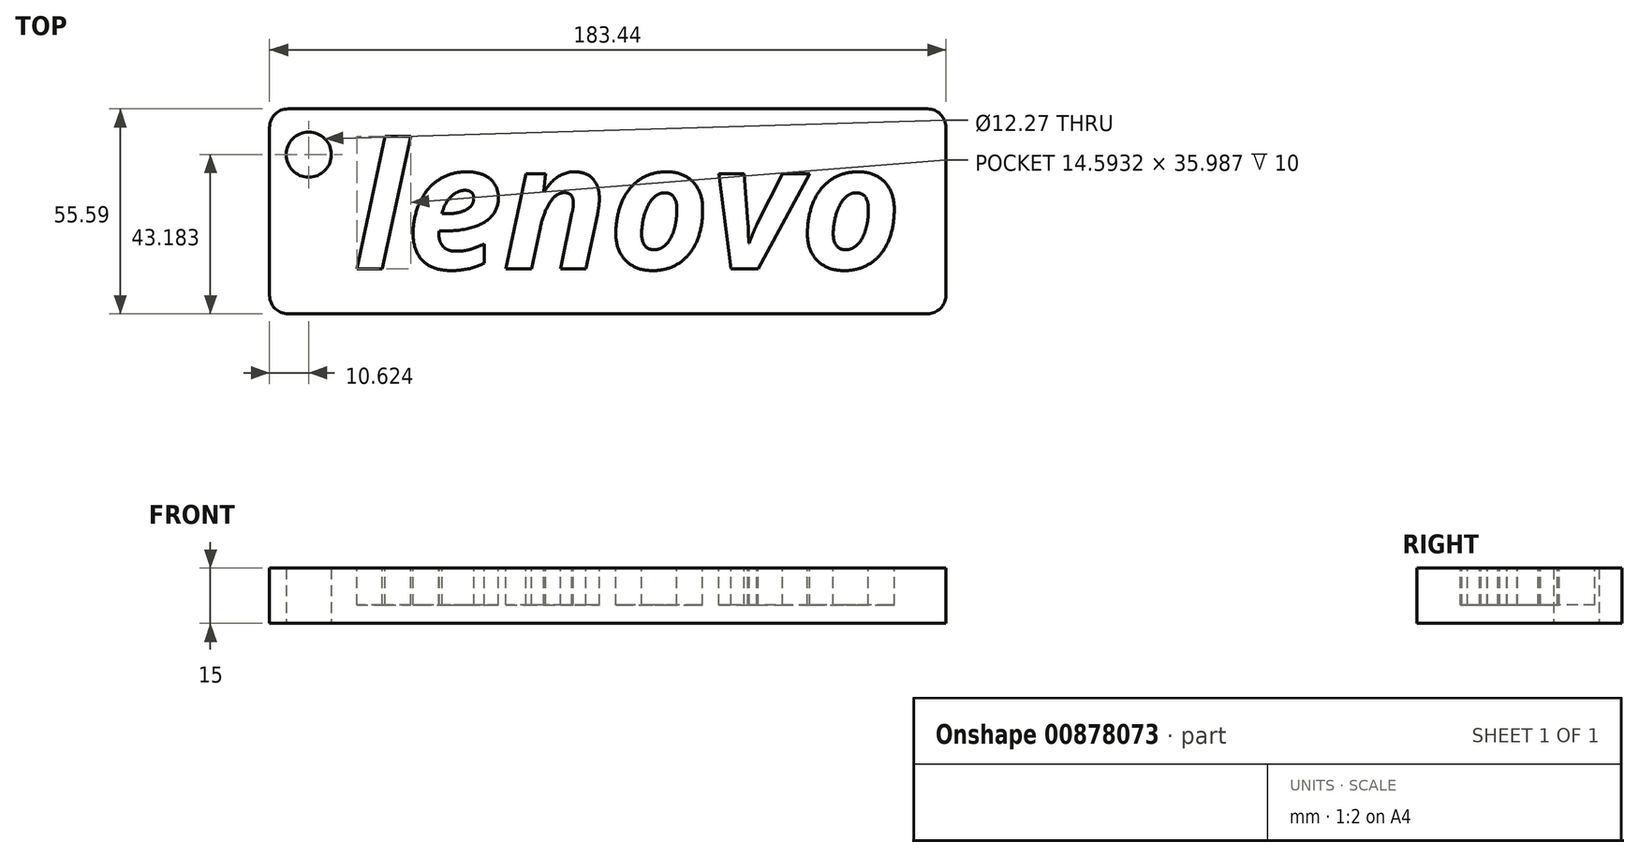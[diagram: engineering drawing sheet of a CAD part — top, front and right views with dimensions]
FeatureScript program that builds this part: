
annotation { "Feature Type Name" : "Feature", "Feature Type Description" : "" }
export const myFeature = defineFeature(function(context is Context, id is Id, definition is map)
    precondition{}
    {
        {
            var Q0;
            Q0=qCreatedBy(makeId("Top.planeOp"),FACE);
            var sketch = newSketch(context, id + "F0", { "sketchPlane" : qUnion([Q0])});
            skLineSegment(sketch, "E0.bottom", {"start": v(-87.4, 49.94) * mm, "end": v(86.04, 49.94) * mm});
            skLineSegment(sketch, "E0.top", {"start": v(-87.4, -5.65) * mm, "end": v(86.04, -5.65) * mm});
            skLineSegment(sketch, "E0.left", {"start": v(-92.4, 44.94) * mm, "end": v(-92.4, -0.65) * mm});
            skLineSegment(sketch, "E0.right", {"start": v(91.04, 44.94) * mm, "end": v(91.04, -0.65) * mm});
            skPoint(sketch, "E1.visualSharp", {"position": v(-92.4, 49.94) * mm});
            skArc(sketch, "E1.filletArc", {"start": v(-87.4, 49.94) * mm, "mid": v(-90.94, 48.47) * mm, "end": v(-92.4, 44.94) * mm});
            skPoint(sketch, "E2.visualSharp", {"position": v(-92.4, -5.65) * mm});
            skArc(sketch, "E2.filletArc", {"start": v(-92.4, -0.65) * mm, "mid": v(-90.94, -4.19) * mm, "end": v(-87.4, -5.65) * mm});
            skPoint(sketch, "E3.visualSharp", {"position": v(91.04, 49.94) * mm});
            skArc(sketch, "E3.filletArc", {"start": v(91.04, 44.94) * mm, "mid": v(89.57, 48.47) * mm, "end": v(86.04, 49.94) * mm});
            skPoint(sketch, "E4.visualSharp", {"position": v(91.04, -5.65) * mm});
            skArc(sketch, "E4.filletArc", {"start": v(86.04, -5.65) * mm, "mid": v(89.57, -4.19) * mm, "end": v(91.04, -0.65) * mm});
            skCircle(sketch, "E5", {"center": v(-81.78, 37.53) * mm, "radius": 6.13 * mm});
            skSolve(sketch);
        }
        {
            var Q0;
            Q0 = qSketchRegion(id + "F0", true);
            extrude(context, id + "F1", {"entities" : qUnion([Q0]), "depth" : 15 * mm, "offsetDistance" : 25 * mm});
        }
        {
            var Q0;
            Q0=qCreatedBy(makeId("Top.planeOp"),FACE);
            cPlane(context, id + "F2", {"entities" : qUnion([Q0]), "cplaneType" : CPlaneType.OFFSET, "offset" : 15 * mm, "width" : 150 * mm, "height" : 150 * mm});
        }
        {
            var Q0;
            Q0=qCreatedBy(id+"F2.planeOp",FACE);
            var sketch = newSketch(context, id + "F3", { "sketchPlane" : qUnion([Q0])});
            skText(sketch, "E6", { "text": "lenovo \n", "fontName": "OpenSans-BoldItalic.ttf"});
            const initialGuessF3  = {"E6": [-0.06961, 0.00653, 1, 0, 0.0341]};
            skSetInitialGuess(sketch, initialGuessF3);
            skSolve(sketch);
        }
        {
            var Q0;
            Q0 = qSketchRegion(id + "F3", true);
            extrude(context, id + "F4", {"entities" : qUnion([Q0]), "operationType" : NewBodyOperationType.REMOVE, "oppositeDirection" : true, "depth" : 10 * mm, "offsetDistance" : 25 * mm});
        }
    });
